# Revit family: xBasin-Wall_Hung-DXV-Lyndon-D20077008.415
name_source: partatom
category: Plumbing Fixtures
revit_build: Autodesk Revit 2014 (Build: 20130308_1515(x64)
units: mm (PartAtom-declared; Revit-internal decimal feet)

## types (1)
- D20077008.415
    ADA Compliant = Yes
    Assembly Code = D2010310
    Basin Shape = Rectangular
    CW Connection = Yes
    CWFU = 1.5
    Cold Water Connection Height = 19 3/4"
    Cold Water Connection Width = 4"
    Cold Water Diameter = 1/2"
    Cold Water Radius = 1/4"
    Default Elevation = 34"
    Description = Lyndon 47" Three-Hole, Wall-Mount Trough Lavatory
    Finish = Fine Fire Clay-DXV-415-Canvas White
    HW Connection = Yes
    HWFU = 1.5
    Height = 8 9/16"
    Hole Location = 11 13/16"
    Hot Water Connection Height = 19 3/4"
    Hot Water Connection Width = 4"
    Hot Water Diameter = 1/2"
    Hot Water Radius = 1/4"
    Installation Type = Wall Hung
    Length = 17 7/16"
    Manufacturer = DXV
    Material = Fine Fire Clay-DXV-415-Canvas White
    Model = D20077008.415
    Revised Date = 02/06/2018
    URL = https://www.dxv.com
    Vent Connection = No
    WFU = 2
    Warranty Documentation Link = https://www.dxv.com
    Waste Connection = Yes
    Waste Connection Diameter = 1 1/4"
    Waste Connection Height = 18 1/8"
    Waste Connection Radius = 5/8"
    Width = 46 3/4"

## geometry (parser evidence)
native form markers: Sweep x2
no freeform markers — native parametric forms only
